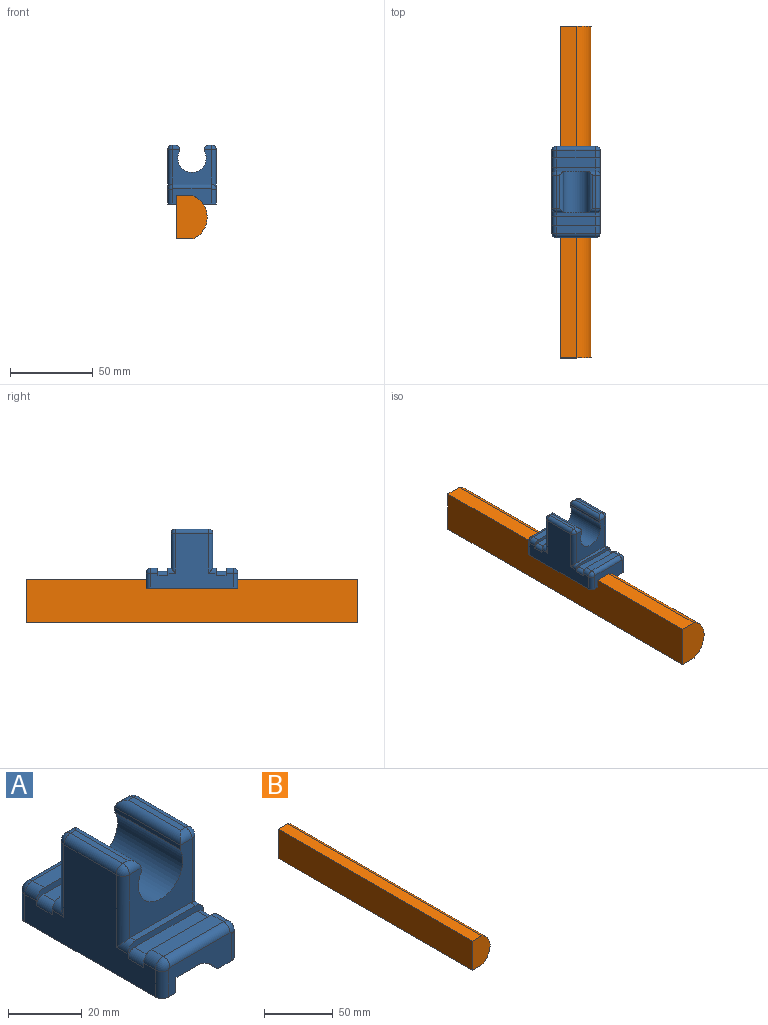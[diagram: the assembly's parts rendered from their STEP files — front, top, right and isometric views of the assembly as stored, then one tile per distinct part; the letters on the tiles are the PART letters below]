
ASSEMBLY  parts=2 mates=1
PART A: 64 faces, bbox 29x55x35.5 mm
  f0: plane 24x9.5mm, normal (0,-1,0), area 161.1mm2, adj f5,f16,f17,f18,f19,f33,f34,f35
  f1: plane 24x9.5mm, normal (0,1,0), area 161.1mm2, adj f5,f16,f17,f18,f19,f30,f31,f32
  f2: plane 23x2mm, normal (0,0,1), area 46mm2, adj f12,f20,f60,f61
  f3: plane 23x4.5mm, normal (0,0,1), area 103.5mm2, adj f24,f31,f52,f54
  f4: plane 50x33mm, normal (1,0,0), area 912mm2, adj f16,f20,f21,f23,f24,f27,f28,f32
  f5: plane 55x5.35mm, normal (0,0,-1), area 291.6mm2, adj f0,f1,f11,f17,f30,f33
  f6: plane 20x2mm, normal (0,0,1), area 40mm2, adj f44,f46,f47,f51
  f7: plane 25x1.5mm, normal (-1,0,0), area 37.5mm2, adj f8,f12,f13,f44
  f8: cylinder r=8.5mm len=25mm, axis (0,1,0), area 875.8mm2, adj f7,f9,f12,f13
  f9: plane 25x1.5mm, normal (1,0,0), area 37.5mm2, adj f8,f12,f13,f43
  f10: plane 20x2mm, normal (0,0,1), area 40mm2, adj f37,f41,f42,f43
  f11: plane 50x33mm, normal (-1,0,0), area 912mm2, adj f5,f20,f21,f23,f24,f26,f29,f30
  f12: plane 24x21.04mm, normal (0,-1,0), area 302.6mm2, adj f2,f7,f8,f9,f36,f41,f45,f46
  f13: plane 24x21.04mm, normal (0,1,0), area 302.6mm2, adj f7,f8,f9,f15,f38,f42,f47,f48
  f14: plane 23x4.5mm, normal (0,0,1), area 103.5mm2, adj f21,f34,f56,f58
  f15: plane 23x2mm, normal (0,0,1), area 46mm2, adj f13,f23,f62,f63
  f16: plane 55x7.83mm, normal (0,0,-1), area 428.2mm2, adj f0,f1,f4,f18,f32,f35
  f17: plane 55x5mm, normal (1,0,0), area 275mm2, adj f0,f1,f5,f19
  f18: cylinder r=14.13mm len=55mm, axis (0,-1,0), area 440.4mm2, adj f0,f1,f16,f19
  f19: plane 55x9.7mm, normal (0,0,-1), area 533.5mm2, adj f0,f1,f17,f18
  f20: plane 29x4.5mm, normal (0,-1,0), area 56.8mm2, adj f2,f4,f11,f22,f26,f27,f60,f61
  f21: plane 29x4.5mm, normal (0,1,0), area 56.8mm2, adj f4,f11,f14,f22,f26,f27,f56,f58
  f22: plane 24x6mm, normal (0,0,1), area 144mm2, adj f20,f21,f26,f27
  f23: plane 29x4.5mm, normal (0,1,0), area 56.8mm2, adj f4,f11,f15,f25,f28,f29,f62,f63
  f24: plane 29x4.5mm, normal (0,-1,0), area 56.8mm2, adj f3,f4,f11,f25,f28,f29,f52,f54
  f25: plane 24x6mm, normal (0,0,1), area 144mm2, adj f23,f24,f28,f29
  f26: cylinder r=2.5mm len=6mm, axis (0,-1,0), area 23.6mm2, adj f11,f20,f21,f22
  f27: cylinder r=2.5mm len=6mm, axis (0,1,0), area 23.6mm2, adj f4,f20,f21,f22
  f28: cylinder r=2.5mm len=6mm, axis (0,1,0), area 23.6mm2, adj f4,f23,f24,f25
  f29: cylinder r=2.5mm len=6mm, axis (0,-1,0), area 23.6mm2, adj f11,f23,f24,f25
  f30: cylinder r=2.5mm len=9mm, axis (0,0,-1), area 35.3mm2, adj f1,f5,f11,f53
  f31: cylinder r=2.5mm len=23mm, axis (-1,0,0), area 90.3mm2, adj f1,f3,f53,f55
  f32: cylinder r=2.5mm len=9mm, axis (0,0,1), area 35.3mm2, adj f1,f4,f16,f55
  f33: cylinder r=2.5mm len=9mm, axis (0,0,1), area 35.3mm2, adj f0,f5,f11,f57
  f34: cylinder r=2.5mm len=23mm, axis (1,0,0), area 90.3mm2, adj f0,f14,f57,f59
  f35: cylinder r=2.5mm len=9mm, axis (0,0,-1), area 35.3mm2, adj f0,f4,f16,f59
  f36: cylinder r=2.5mm len=24mm, axis (0,0,1), area 87.2mm2, adj f11,f12,f39,f61
  f37: cylinder r=2.5mm len=20mm, axis (0,-1,0), area 78.5mm2, adj f10,f11,f39,f40
  f38: cylinder r=2.5mm len=24mm, axis (0,0,-1), area 87.2mm2, adj f11,f13,f40,f63
  f39: sphere r=2.5mm, area 9.8mm2, adj f36,f37,f41
  f40: sphere r=2.5mm, area 9.8mm2, adj f37,f38,f42
  f41: cylinder r=2.5mm len=4.5mm, axis (1,0,0), area 14.1mm2, adj f10,f12,f39,f43
  f42: cylinder r=2.5mm len=4.5mm, axis (-1,0,0), area 14.1mm2, adj f10,f13,f40,f43
  f43: cylinder r=2.5mm len=25mm, axis (0,1,0), area 91mm2, adj f9,f10,f41,f42
  f44: cylinder r=2.5mm len=25mm, axis (0,1,0), area 91mm2, adj f6,f7,f46,f47
  f45: cylinder r=2.5mm len=24mm, axis (0,0,-1), area 87.2mm2, adj f4,f12,f49,f60
  f46: cylinder r=2.5mm len=4.5mm, axis (1,0,0), area 14.1mm2, adj f6,f12,f44,f49
  f47: cylinder r=2.5mm len=4.5mm, axis (-1,0,0), area 14.1mm2, adj f6,f13,f44,f50
  f48: cylinder r=2.5mm len=24mm, axis (0,0,1), area 87.2mm2, adj f4,f13,f50,f62
  f49: sphere r=2.5mm, area 9.8mm2, adj f45,f46,f51
  f50: sphere r=2.5mm, area 9.8mm2, adj f47,f48,f51
  f51: cylinder r=2.5mm len=20mm, axis (0,-1,0), area 78.5mm2, adj f4,f6,f49,f50
  f52: cylinder r=3mm len=4.5mm, axis (0,-1,0), area 21.2mm2, adj f3,f11,f24,f53
  f53: torus R=0.5mm, axis (0,-1,0), area 12.9mm2, adj f1,f30,f31,f52
  f54: cylinder r=3mm len=4.5mm, axis (0,1,0), area 21.2mm2, adj f3,f4,f24,f55
  f55: torus R=0.5mm, axis (0,-1,0), area 12.9mm2, adj f1,f31,f32,f54
  f56: cylinder r=3mm len=4.5mm, axis (0,-1,0), area 21.2mm2, adj f11,f14,f21,f57
  f57: torus R=0.5mm, axis (0,-1,0), area 12.9mm2, adj f0,f33,f34,f56
  f58: cylinder r=3mm len=4.5mm, axis (0,1,0), area 21.2mm2, adj f4,f14,f21,f59
  f59: torus R=0.5mm, axis (0,-1,0), area 12.9mm2, adj f0,f34,f35,f58
  f60: cylinder r=3mm len=4.5mm, axis (0,1,0), area 13.3mm2, adj f2,f4,f12,f20,f45
  f61: cylinder r=3mm len=4.5mm, axis (0,-1,0), area 13.3mm2, adj f2,f11,f12,f20,f36
  f62: cylinder r=3mm len=4.5mm, axis (0,1,0), area 13.3mm2, adj f4,f13,f15,f23,f48
  f63: cylinder r=3mm len=4.5mm, axis (0,-1,0), area 13.3mm2, adj f11,f13,f15,f23,f38
PART B: 6 faces, bbox 18.3x200x26 mm
  f0: plane 200x26mm, normal (-1,0,0), area 5200mm2, adj f1,f3,f4,f5
  f1: plane 200x9.7mm, normal (0,0,-1), area 1940mm2, adj f0,f2,f4,f5
  f2: cylinder r=14.13mm len=200mm, axis (0,1,0), area 6604.5mm2, adj f1,f3,f4,f5
  f3: plane 200x9.7mm, normal (0,0,1), area 1940mm2, adj f0,f2,f4,f5
  f4: plane 26x18.3mm, normal (0,-1,0), area 413.6mm2, adj f0,f1,f2,f3
  f5: plane 26x18.3mm, normal (0,1,0), area 413.6mm2, adj f0,f1,f2,f3
PLACE A t=(0,0,5)mm
PLACE B t=(0,87.5,-30.5)mm
MATE fastened A.f19 <-> B.f3  axis (0,0,-1) through (-4.3,-12.5,-17.5)mm
